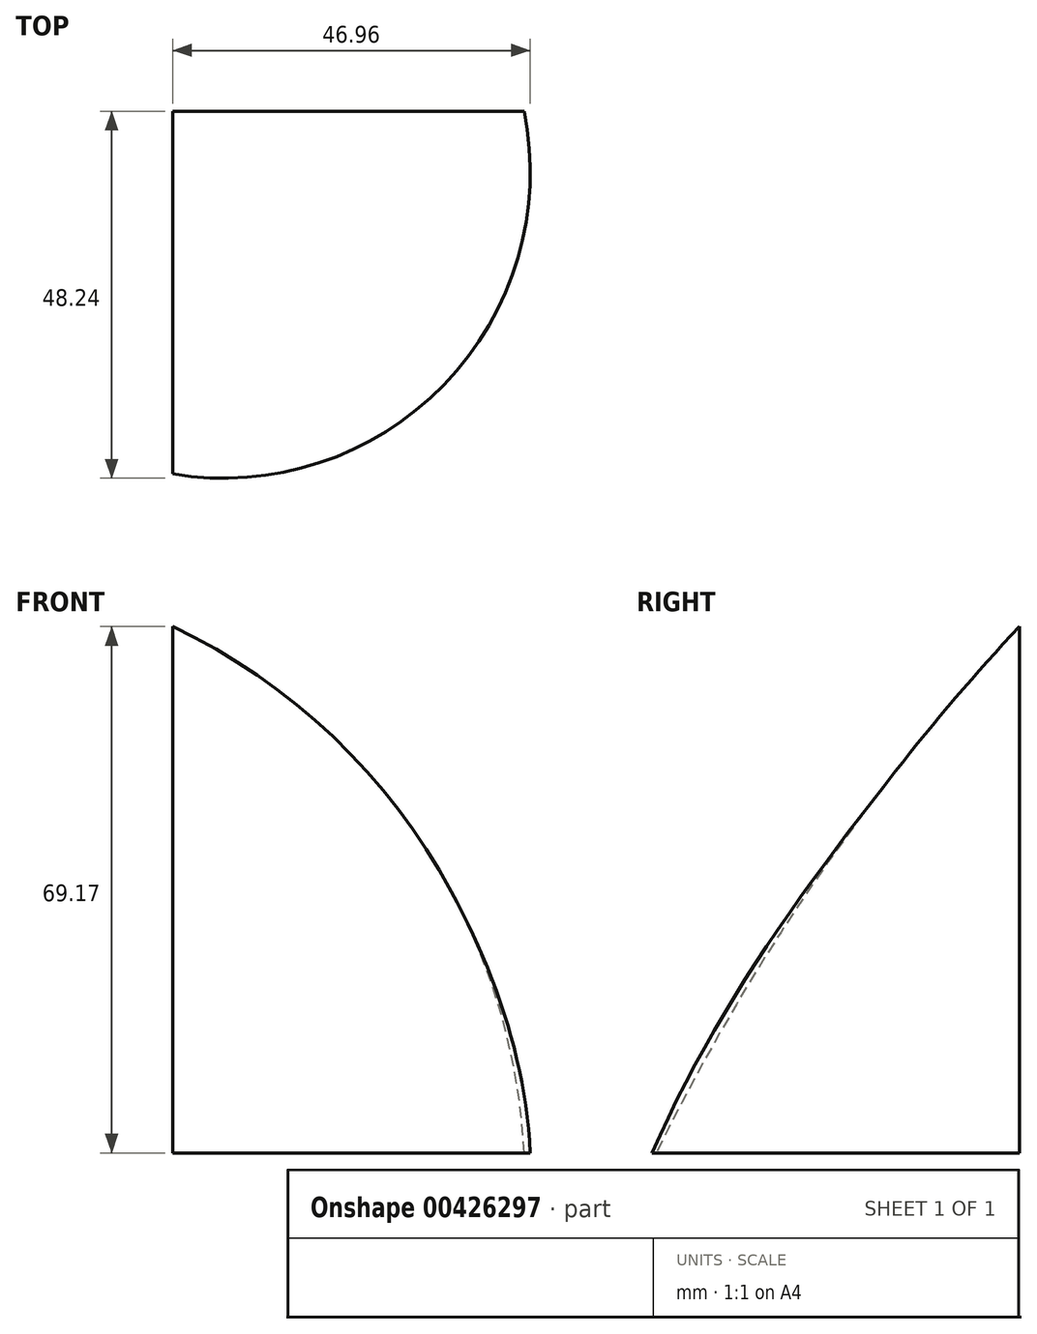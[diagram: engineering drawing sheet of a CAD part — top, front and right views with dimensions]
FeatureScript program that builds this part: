
annotation { "Feature Type Name" : "Feature", "Feature Type Description" : "" }
export const myFeature = defineFeature(function(context is Context, id is Id, definition is map)
    precondition{}
    {
        {
            var Q0;
            Q0=qCreatedBy(makeId("Front.planeOp"),FACE);
            var sketch = newSketch(context, id + "F0", { "sketchPlane" : qUnion([Q0])});
            skArc(sketch, "E0", {"start": v(46.17, 0) * mm, "mid": v(32.63, 40.96) * mm, "end": v(0, 69.17) * mm});
            skLineSegment(sketch, "E1", {"start": v(0, 0) * mm, "end": v(0, 97.21) * mm, "construction": true});
            skArc(sketch, "E2.MirrorCS", {"start": v(-46.17, 0) * mm, "mid": v(-32.63, 40.96) * mm, "end": v(0, 69.17) * mm});
            skSolve(sketch);
        }
        {
            var Q0;
            Q0=qCreatedBy(makeId("Right.planeOp"),FACE);
            var sketch = newSketch(context, id + "F1", { "sketchPlane" : qUnion([Q0])});
            skArc(sketch, "E3", {"start": v(0, 69.17) * mm, "mid": v(-26.41, 36.36) * mm, "end": v(-47.68, 0) * mm});
            skSolve(sketch);
        }
        {
            var Q0;
            Q0=qCreatedBy(makeId("Top.planeOp"),FACE);
            var sketch = newSketch(context, id + "F2", { "sketchPlane" : qUnion([Q0])});
            skArc(sketch, "E4", {"start": v(0, -47.68) * mm, "mid": v(35.62, -35.98) * mm, "end": v(46.17, 0) * mm});
            skSolve(sketch);
        }
        {
            var Q0;
            Q0=sQuery(id+"F1.wireOp",EDGE,"E3");
            var Q1;
            Q1=sQuery(id+"F0.wireOp",EDGE,"E0");
            var Q2;
            Q2=sQuery(id+"F2.wireOp",EDGE,"E4");
            loft(context, id + "F3", {"bodyType" : ToolBodyType.SURFACE, "addGuides" : true, "wireProfilesArray" : [{ "wireProfileEntities" : qUnion([Q0]) }, { "wireProfileEntities" : qUnion([Q1]) }], "guidesArray" : [{ "guideEntities" : qUnion([Q2]), "guideDerivativeType" : LoftGuideDerivativeType.DEFAULT, "guideDerivativeMagnitude" : 1 }]});
        }
    });
